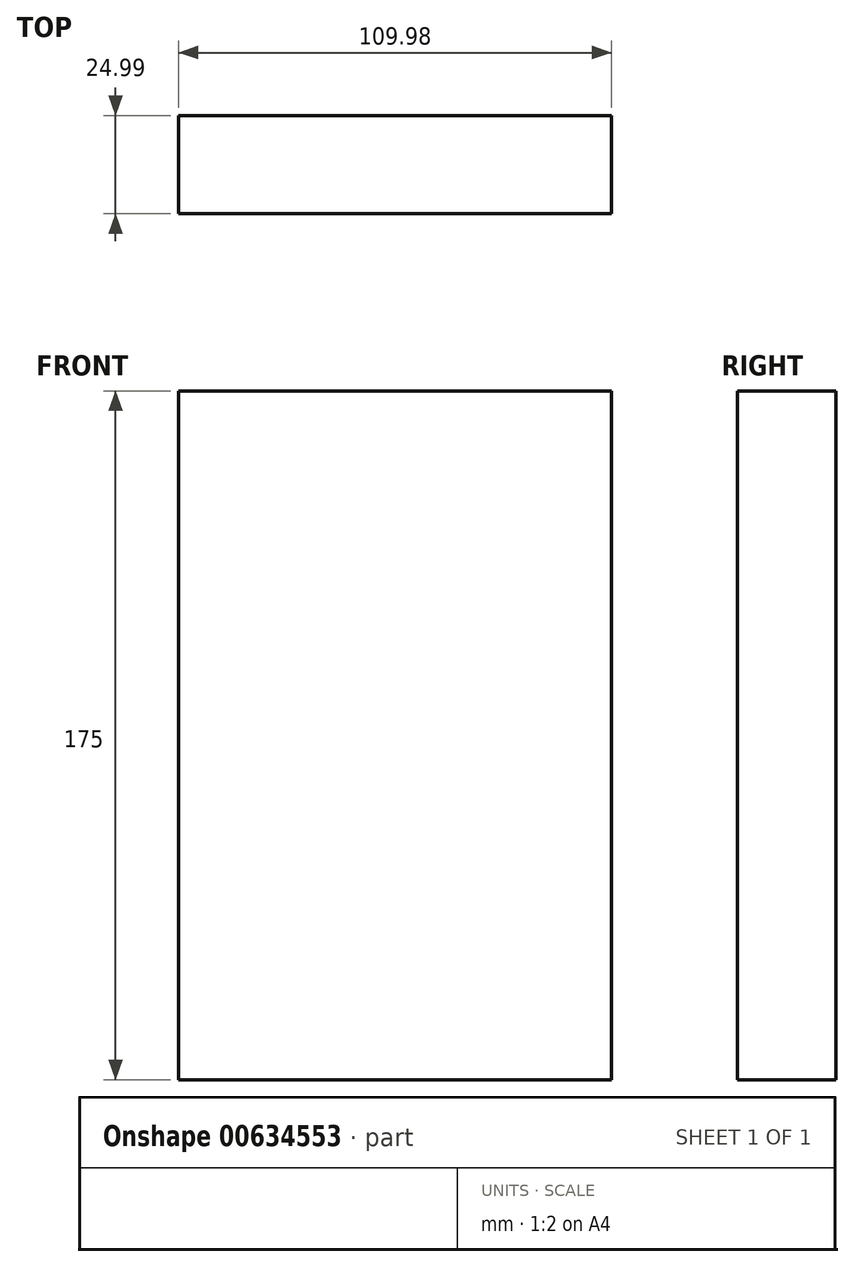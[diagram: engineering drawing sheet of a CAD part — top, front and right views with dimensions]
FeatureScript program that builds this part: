
annotation { "Feature Type Name" : "Feature", "Feature Type Description" : "" }
export const myFeature = defineFeature(function(context is Context, id is Id, definition is map)
    precondition{}
    {
        {
            var Q0;
            Q0=qCreatedBy(makeId("Front.planeOp"),FACE);
            var sketch = newSketch(context, id + "F0", { "sketchPlane" : qUnion([Q0])});
            skLineSegment(sketch, "E0", {"start": v(-41.8, 91.72) * mm, "end": v(-41.8, -83.28) * mm});
            skLineSegment(sketch, "E1", {"start": v(-41.8, 91.72) * mm, "end": v(68.18, 91.72) * mm});
            skLineSegment(sketch, "E2", {"start": v(68.18, 91.72) * mm, "end": v(68.18, -83.28) * mm});
            skLineSegment(sketch, "E3", {"start": v(68.18, -83.28) * mm, "end": v(-41.8, -83.28) * mm});
            skSolve(sketch);
        }
        {
            var Q0;
            Q0=makeQuery(id+"F0.imprint","IMPRINT",FACE,{"disambiguationData":[TD([[makeQuery(id+"F0.imprint","IMPRINT",EDGE,{"derivedFrom":sQuery(id+"F0.wireOp",EDGE,"E0")}),1.0]])]});
            extrude(context, id + "F1", {"entities" : qUnion([Q0]), "depth" : 25 * mm, "offsetDistance" : 25.4 * mm});
        }
    });
